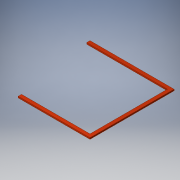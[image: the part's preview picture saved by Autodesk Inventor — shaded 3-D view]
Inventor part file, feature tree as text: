
AUTODESK INVENTOR PART (.ipt)
format: ipt  version: 2016 (Build 200138000, 138)  size: 106,496 bytes
history: native  units: in
note: dims shown in document units (in); Inventor stores cm internally (conversion verified against a paired STEP export)
features: extrude x1
ambient origin geometry x8: Origin, YZ Plane, XZ Plane, XY Plane, X Axis, Y Axis, Z Axis, Center Point
bodies: Solid1 (feature_tree)
feature tree (1):
  extrude  "Extrusion1"  Depth=3.5in
